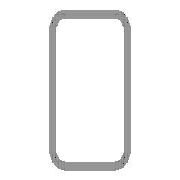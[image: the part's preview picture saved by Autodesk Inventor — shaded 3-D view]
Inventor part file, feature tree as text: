
AUTODESK INVENTOR PART (.ipt)
format: ipt  version: 2022 (Build 260153000, 153)  size: 218,624 bytes
history: native  units: mm (DEFAULTED — no unit token found)
features: other x5, sketch x3, plane x1
ambient origin geometry x8: Origin, YZ Plane, XZ Plane, XY Plane, X Axis, Y Axis, Z Axis, Center Point
bodies: Solid1 (feature_tree), Body (feature_tree), Solid6 (feature_tree)
feature tree (9):
  parser-record x1  (decoder bookkeeping rows leaked as tree rows — omitted from the tree; the rows remain in map.json)
  other  "Driven Length"
  other  "Start Plane"
  other  "End Plane"
  sketch  "Sketch"  dims[d7=7.5mm d10=50.0mm d11=30.0mm d12=5.0mm d13=-22.0mm d14=202.0mm d15=25.0mm d16=15.0mm d17=90.0deg d18=224.0mm]
  sketch  "Sketch3"  dims[d3=224.0mm]
  plane  "Work Plane3"
  sketch  "Sketch4"  dims[d4=0.0mm]
  other  "Srf5"
